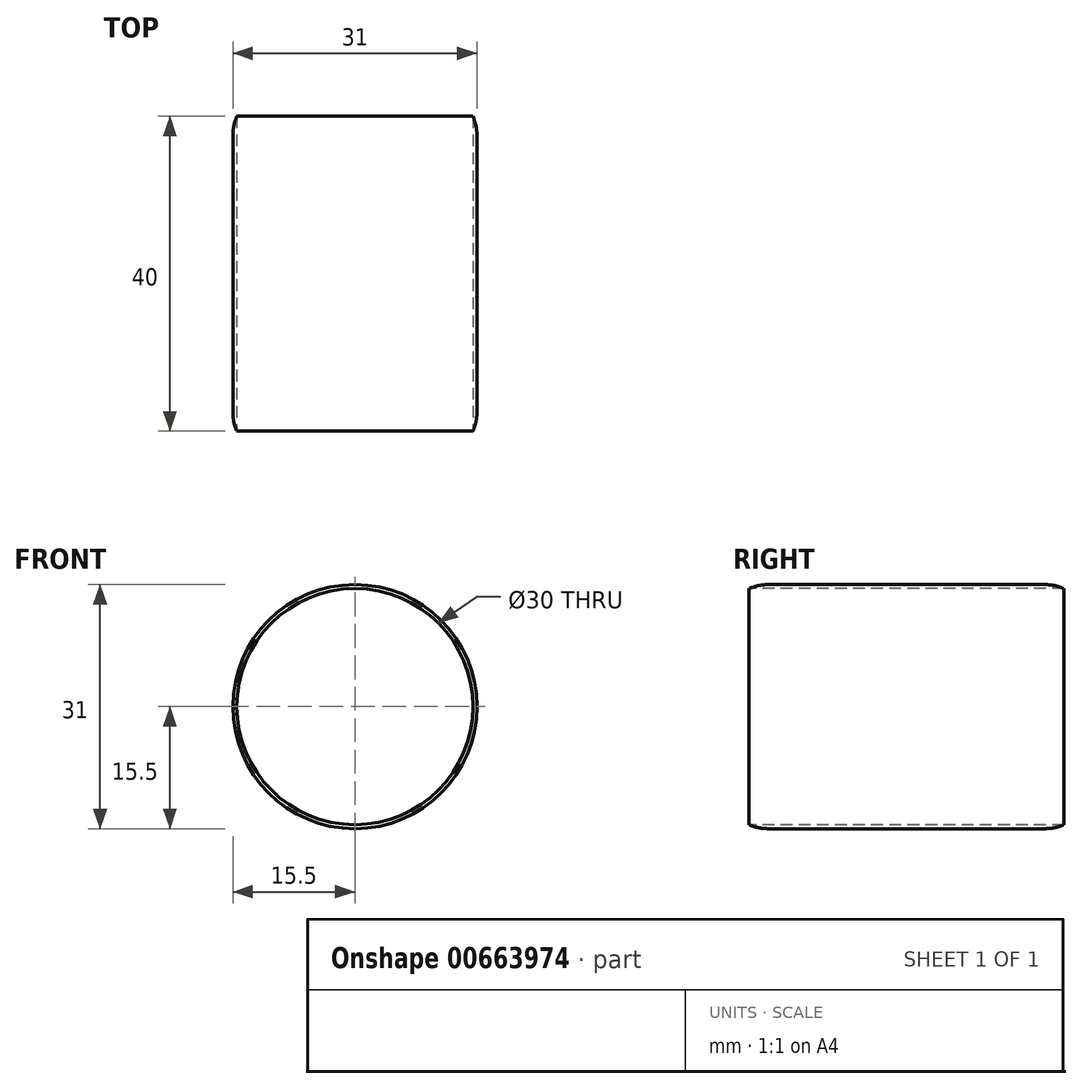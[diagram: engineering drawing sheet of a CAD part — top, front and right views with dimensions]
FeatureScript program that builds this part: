
annotation { "Feature Type Name" : "Feature", "Feature Type Description" : "" }
export const myFeature = defineFeature(function(context is Context, id is Id, definition is map)
    precondition{}
    {
        {
            var Q0;
            Q0=qCreatedBy(makeId("Front.planeOp"),FACE);
            var sketch = newSketch(context, id + "F0", { "sketchPlane" : qUnion([Q0])});
            skCircle(sketch, "E0", {"center": v(0, 0) * mm, "radius": 15.5 * mm});
            skSolve(sketch);
        }
        {
            var Q0;
            Q0 = qSketchRegion(id + "F0", true);
            extrude(context, id + "F1", {"entities" : qUnion([Q0]), "depth" : 40 * mm, "offsetDistance" : 25 * mm});
        }
        {
            var Q0;
            Q0=makeQuery(id+"F1.opExtrude","CAP_FACE",FACE,{"disambiguationData":[OSD([sQuery(id+"F0.wireOp",EDGE,"E0")])],"isStart":false});
            var sketch = newSketch(context, id + "F2", { "sketchPlane" : qUnion([Q0])});
            skCircle(sketch, "E1", {"center": v(0, 0) * mm, "radius": 15 * mm});
            skSolve(sketch);
        }
        {
            var Q0;
            Q0 = qSketchRegion(id + "F2", true);
            extrude(context, id + "F3", {"entities" : qUnion([Q0]), "operationType" : NewBodyOperationType.REMOVE, "oppositeDirection" : true, "depth" : 40 * mm, "offsetDistance" : 25 * mm});
        }
        {
            var Q0;
            Q0=makeQuery(id+"F1.opExtrude","CAP_EDGE",EDGE,{"disambiguationData":[OSD([sQuery(id+"F0.wireOp",EDGE,"E0")])],"isStart":false});
            fillet(context, id + "F4", {"entities" : qUnion([Q0]), "radius" : 6 * mm, "tangentPropagation" : true, "allowEdgeOverflow" : false});
        }
        {
            var Q0;
            Q0=makeQuery(id+"F1.opExtrude","CAP_EDGE",EDGE,{"disambiguationData":[OSD([sQuery(id+"F0.wireOp",EDGE,"E0")])],"isStart":true});
            fillet(context, id + "F5", {"entities" : qUnion([Q0]), "radius" : 6 * mm, "tangentPropagation" : true, "allowEdgeOverflow" : false});
        }
    });
